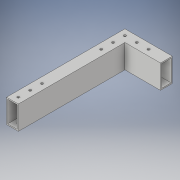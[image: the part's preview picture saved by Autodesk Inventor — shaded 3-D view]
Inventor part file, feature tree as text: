
AUTODESK INVENTOR PART (.ipt)
format: ipt  version: 2018 (Build 220112000, 112)  size: 181,760 bytes
history: native  units: in
note: dims shown in document units (in); Inventor stores cm internally (conversion verified against a paired STEP export)
features: extrude x5, sketch x5
ambient origin geometry x8: Origin, YZ Plane, XZ Plane, XY Plane, X Axis, Y Axis, Z Axis, Center Point
bodies: Body1 (feature_tree)
feature tree (10):
  extrude  "Extrusion12"  Depth=2.0in
  extrude  "Extrusion14"  Depth=0.1in
  extrude  "Extrusion16"  Depth=0.1in
  extrude  "Extrusion17"  Depth=0.1in TaperAngle=0.0deg
  extrude  "Extrusion18"  TaperAngle=0.0deg  [1 undecoded]
  sketch  "Sketch15"  dims[d46=1.0in d47=2.0in]
  sketch  "Sketch17"  dims[d48=0.1in d49=0.1in]
  sketch  "Sketch20"  dims[d50=0.1in d51=0.1in]
  sketch  "Sketch21"  dims[d52=3.0in d53=0.0in d62=0.1in d63=0.0in]
  sketch  "Sketch22"  dims[d71=1.0in d72=2.0in d73=0.1in d74=0.1in d75=0.1in d76=0.1in d77=0.1in d78=0.0in d79=10.0in d80=0.0in d81=0.5in d82=0.5in d83=0.5in d84=1.0in d85=0.5in d86=0.2031in d87=0.2031in d88=0.2031in d89=1.0in d90=1.0in d91=1.0in d92=0.2031in d93=0.2031in d94=0.5in d95=0.5in d96=3.0in d97=0.0in d98=1.0in d99=1.0in d100=0.5in d101=0.5in d102=0.5in d103=0.2031in d104=0.2031in d105=0.2031in d106=3.0in d107=0.0in d108=0.5in]
note: 1 required parameter value undecoded (feature->parameter linkage not recoverable at this tier; creation-order binding heuristic only, values carry confidence <= 0.55)
